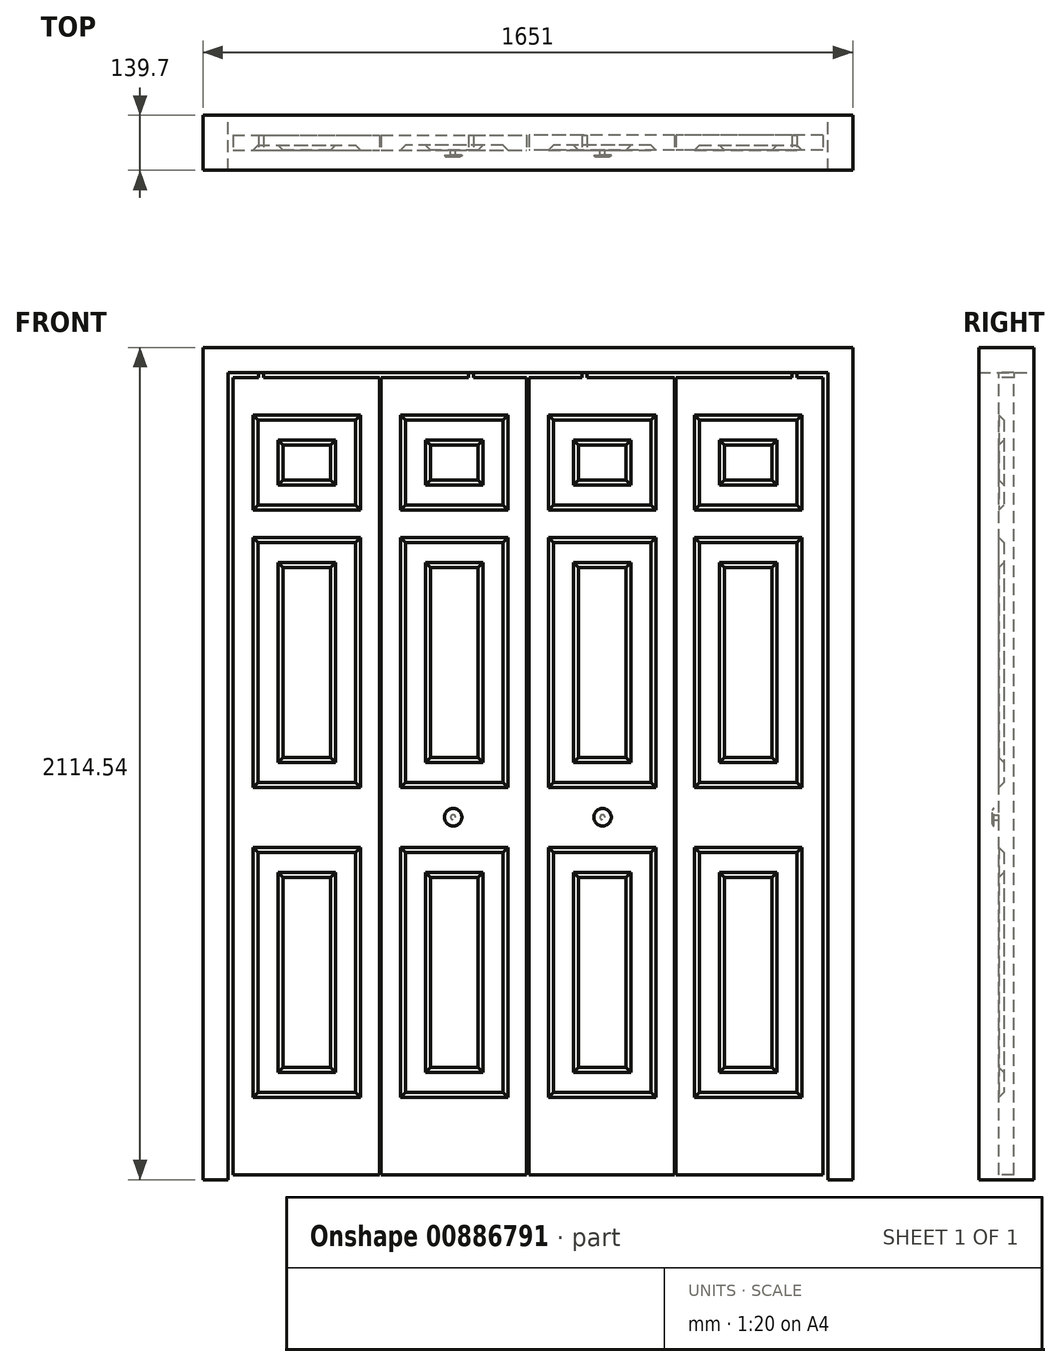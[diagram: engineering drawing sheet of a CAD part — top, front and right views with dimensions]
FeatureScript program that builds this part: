
annotation { "Feature Type Name" : "Feature", "Feature Type Description" : "" }
export const myFeature = defineFeature(function(context is Context, id is Id, definition is map)
    precondition{}
    {
        {
            var Q0;
            Q0=qCreatedBy(makeId("Front.planeOp"),FACE);
            var sketch = newSketch(context, id + "F0", { "sketchPlane" : qUnion([Q0])});
            skLineSegment(sketch, "E0.bottom", {"start": v(-825.5, 1057.28) * mm, "end": v(825.5, 1057.28) * mm});
            skLineSegment(sketch, "E0.top", {"start": v(-825.5, -1057.28) * mm, "end": v(-762, -1057.28) * mm});
            skLineSegment(sketch, "E0.left", {"start": v(-825.5, 1057.28) * mm, "end": v(-825.5, -1057.28) * mm});
            skLineSegment(sketch, "E0.right", {"start": v(825.5, 1057.28) * mm, "end": v(825.5, -1057.28) * mm});
            skPoint(sketch, "E0.middle", {"position": v(0, 0) * mm});
            skLineSegment(sketch, "E1", {"start": v(-762, -1057.28) * mm, "end": v(-762, 993.78) * mm});
            skLineSegment(sketch, "E2", {"start": v(-762, 993.78) * mm, "end": v(762, 993.78) * mm});
            skLineSegment(sketch, "E3", {"start": v(762, 993.78) * mm, "end": v(762, -1057.28) * mm});
            skLineSegment(sketch, "E4.trimOffspring", {"start": v(762, -1057.28) * mm, "end": v(825.5, -1057.28) * mm});
            skLineSegment(sketch, "E5", {"start": v(-762, -1057.28) * mm, "end": v(762, -1057.28) * mm});
            skSolve(sketch);
        }
        {
            var Q0;
            Q0=makeQuery(id+"F0.imprint","IMPRINT",FACE,{"disambiguationData":[TD([[makeQuery(id+"F0.imprint","IMPRINT",EDGE,{"derivedFrom":sQuery(id+"F0.wireOp",EDGE,"E0.bottom")}),-1.0]])]});
            extrude(context, id + "F1", {"entities" : qUnion([Q0]), "endBound" : BoundingType.SYMMETRIC, "depth" : 139.7 * mm, "offsetDistance" : 25.4 * mm});
        }
        {
            var Q0;
            Q0=makeQuery(id+"F0.imprint","IMPRINT",FACE,{"disambiguationData":[TD([[makeQuery(id+"F0.imprint","IMPRINT",EDGE,{"derivedFrom":sQuery(id+"F0.wireOp",EDGE,"E1")}),-1.0]])]});
            extrude(context, id + "F2", {"entities" : qUnion([Q0]), "operationType" : NewBodyOperationType.ADD, "endBound" : BoundingType.SYMMETRIC, "depth" : 38.1 * mm, "offsetDistance" : 25.4 * mm});
        }
        {
            var Q0;
            Q0=makeQuery(id+"F2.opExtrude","CAP_FACE",FACE,{"disambiguationData":[OSD([sQuery(id+"F0.wireOp",EDGE,"E1"),sQuery(id+"F0.wireOp",EDGE,"E2"),sQuery(id+"F0.wireOp",EDGE,"E3"),sQuery(id+"F0.wireOp",EDGE,"E5")])],"isStart":false});
            var sketch = newSketch(context, id + "F3", { "sketchPlane" : qUnion([Q0])});
            skLineSegment(sketch, "E6", {"start": v(-749.3, -1044.58) * mm, "end": v(-749.3, 981.08) * mm});
            skLineSegment(sketch, "E7", {"start": v(-749.3, 981.08) * mm, "end": v(-683.85, 981.08) * mm});
            skLineSegment(sketch, "E8", {"start": v(-683.85, 981.08) * mm, "end": v(-683.85, 993.78) * mm});
            skLineSegment(sketch, "E9", {"start": v(-671.15, 993.78) * mm, "end": v(-671.15, 981.08) * mm});
            skLineSegment(sketch, "E10", {"start": v(-671.15, 981.08) * mm, "end": v(-150.18, 981.08) * mm});
            skLineSegment(sketch, "E11", {"start": v(-150.18, 981.08) * mm, "end": v(-150.18, 993.78) * mm});
            skLineSegment(sketch, "E12", {"start": v(-137.48, 993.78) * mm, "end": v(-137.48, 981.08) * mm});
            skLineSegment(sketch, "E13", {"start": v(-137.48, 981.08) * mm, "end": v(0, 981.08) * mm});
            skLineSegment(sketch, "E14", {"start": v(-749.3, -1044.58) * mm, "end": v(0, -1044.58) * mm});
            skLineSegment(sketch, "E15", {"start": v(0, 241.91) * mm, "end": v(0, -156.2) * mm});
            skLineSegment(sketch, "E16.MirrorCS", {"start": v(137.48, 993.78) * mm, "end": v(137.48, 981.08) * mm});
            skLineSegment(sketch, "E17.MirrorCS", {"start": v(671.15, 993.78) * mm, "end": v(671.15, 981.08) * mm});
            skLineSegment(sketch, "E18.MirrorCS", {"start": v(749.3, 981.08) * mm, "end": v(683.85, 981.08) * mm});
            skLineSegment(sketch, "E19.MirrorCS", {"start": v(683.85, 981.08) * mm, "end": v(683.85, 993.78) * mm});
            skLineSegment(sketch, "E20.MirrorCS", {"start": v(150.18, 981.08) * mm, "end": v(150.18, 993.78) * mm});
            skLineSegment(sketch, "E21.MirrorCS", {"start": v(671.15, 981.08) * mm, "end": v(150.18, 981.08) * mm});
            skLineSegment(sketch, "E22.MirrorCS", {"start": v(137.48, 981.08) * mm, "end": v(0, 981.08) * mm});
            skLineSegment(sketch, "E23.MirrorCS", {"start": v(749.3, -1044.58) * mm, "end": v(749.3, 981.08) * mm});
            skLineSegment(sketch, "E24.MirrorCS", {"start": v(749.3, -1044.58) * mm, "end": v(0, -1044.58) * mm});
            skLineSegment(sketch, "E25", {"start": v(-3.17, -1044.58) * mm, "end": v(-3.18, 981.08) * mm});
            skLineSegment(sketch, "E26", {"start": v(3.18, -1044.58) * mm, "end": v(3.17, 981.08) * mm});
            skSolve(sketch);
        }
        {
            var Q0;
            Q0 = qSketchRegion(id + "F3", true);
            var Q1;
            {var subQ7=sQuery(id+"F3.wireOp",EDGE,"E6");Q1=makeQuery(id+"F3.imprint","IMPRINT",FACE,{"disambiguationData":[TD([[makeQuery(id+"F3.imprint","IMPRINT",EDGE,{"derivedFrom":subQ7}),1.0]])]});}
            var Q2;
            {var subQ0=sQuery(id+"F3.wireOp",EDGE,"E17.MirrorCS");Q2=makeQuery(id+"F3.imprint","IMPRINT",FACE,{"disambiguationData":[TD([[makeQuery(id+"F3.imprint","IMPRINT",EDGE,{"derivedFrom":subQ0}),-1.0]])]});}
            var Q3;
            {var subQ4=sQuery(id+"F3.wireOp",EDGE,"E12");Q3=makeQuery(id+"F3.imprint","IMPRINT",FACE,{"disambiguationData":[TD([[makeQuery(id+"F3.imprint","IMPRINT",EDGE,{"derivedFrom":subQ4}),1.0]])]});}
            var Q4;
            {var subQ0=sQuery(id+"F3.wireOp",EDGE,"E9");Q4=makeQuery(id+"F3.imprint","IMPRINT",FACE,{"disambiguationData":[TD([[makeQuery(id+"F3.imprint","IMPRINT",EDGE,{"derivedFrom":subQ0}),1.0]])]});}
            extrude(context, id + "F4", {"entities" : qUnion([Q0, Q1, Q2, Q3, Q4]), "operationType" : NewBodyOperationType.REMOVE, "endBound" : BoundingType.THROUGH_ALL, "oppositeDirection" : true, "depth" : 25.4 * mm, "offsetDistance" : 25.4 * mm});
        }
        {
            var Q0;
            {var subQ1=sQuery(id+"F0.wireOp",EDGE,"E2");var subQ6=sQuery(id+"F0.wireOp",EDGE,"E1");var subQ7=sQuery(id+"F0.wireOp",EDGE,"E3");Q0=makeQuery(id+"F4.boolean.opBoolean","SPLIT",FACE,{"disambiguationData":[TD([makeQuery(id+"F4.opExtrude","SWEPT_FACE",FACE,{"disambiguationData":[OSD([sQuery(id+"F3.wireOp",EDGE,"E6")])]})])],"derivedFrom":makeQuery(id+"F2.opExtrude","CAP_FACE",FACE,{"disambiguationData":[OSD([subQ6,subQ1,subQ7,sQuery(id+"F0.wireOp",EDGE,"E5")])],"isStart":false})});}
            var sketch = newSketch(context, id + "F5", { "sketchPlane" : qUnion([Q0])});
            skLineSegment(sketch, "E27.bottom", {"start": v(-685.8, 873.12) * mm, "end": v(-438.15, 873.12) * mm});
            skLineSegment(sketch, "E27.top", {"start": v(-685.8, 657.23) * mm, "end": v(-438.15, 657.23) * mm});
            skLineSegment(sketch, "E27.left", {"start": v(-685.8, 873.12) * mm, "end": v(-685.8, 657.23) * mm});
            skLineSegment(sketch, "E27.right", {"start": v(-438.15, 873.12) * mm, "end": v(-438.15, 657.23) * mm});
            skLineSegment(sketch, "E28.bottom", {"start": v(-685.8, 561.98) * mm, "end": v(-438.15, 561.98) * mm});
            skLineSegment(sketch, "E28.top", {"start": v(-685.8, -47.62) * mm, "end": v(-438.15, -47.62) * mm});
            skLineSegment(sketch, "E28.left", {"start": v(-685.8, 561.98) * mm, "end": v(-685.8, -47.62) * mm});
            skLineSegment(sketch, "E28.right", {"start": v(-438.15, 561.98) * mm, "end": v(-438.15, -47.62) * mm});
            skLineSegment(sketch, "E29.bottom", {"start": v(-438.15, -225.42) * mm, "end": v(-685.8, -225.42) * mm});
            skLineSegment(sketch, "E29.top", {"start": v(-438.15, -835.02) * mm, "end": v(-685.8, -835.02) * mm});
            skLineSegment(sketch, "E29.left", {"start": v(-438.15, -225.42) * mm, "end": v(-438.15, -835.02) * mm});
            skLineSegment(sketch, "E29.right", {"start": v(-685.8, -225.42) * mm, "end": v(-685.8, -835.02) * mm});
            skLineSegment(sketch, "E30", {"start": v(-374.65, 943.32) * mm, "end": v(-374.65, -1018.84) * mm});
            skLineSegment(sketch, "E31.0", {"start": v(-635, 511.18) * mm, "end": v(-635, 3.18) * mm});
            skLineSegment(sketch, "E31.1", {"start": v(-635, 511.18) * mm, "end": v(-488.95, 511.18) * mm});
            skLineSegment(sketch, "E31.2", {"start": v(-488.95, 511.18) * mm, "end": v(-488.95, 3.18) * mm});
            skLineSegment(sketch, "E31.3", {"start": v(-635, 3.18) * mm, "end": v(-488.95, 3.18) * mm});
            skLineSegment(sketch, "E32.0", {"start": v(-635, 822.33) * mm, "end": v(-635, 708.03) * mm});
            skLineSegment(sketch, "E32.1", {"start": v(-635, 822.33) * mm, "end": v(-488.95, 822.33) * mm});
            skLineSegment(sketch, "E32.2", {"start": v(-488.95, 822.33) * mm, "end": v(-488.95, 708.03) * mm});
            skLineSegment(sketch, "E32.3", {"start": v(-635, 708.03) * mm, "end": v(-488.95, 708.03) * mm});
            skLineSegment(sketch, "E33.0", {"start": v(-635, -276.22) * mm, "end": v(-635, -784.22) * mm});
            skLineSegment(sketch, "E33.1", {"start": v(-488.95, -276.22) * mm, "end": v(-635, -276.22) * mm});
            skLineSegment(sketch, "E33.2", {"start": v(-488.95, -276.22) * mm, "end": v(-488.95, -784.22) * mm});
            skLineSegment(sketch, "E33.3", {"start": v(-488.95, -784.22) * mm, "end": v(-635, -784.22) * mm});
            skLineSegment(sketch, "E34.MirrorCS", {"start": v(-311.15, -225.42) * mm, "end": v(-311.15, -835.02) * mm});
            skLineSegment(sketch, "E35.MirrorCS", {"start": v(-260.35, 511.18) * mm, "end": v(-260.35, 3.18) * mm});
            skLineSegment(sketch, "E36.MirrorCS", {"start": v(-311.15, -835.02) * mm, "end": v(-63.5, -835.02) * mm});
            skLineSegment(sketch, "E37.MirrorCS", {"start": v(-114.3, 3.18) * mm, "end": v(-260.35, 3.18) * mm});
            skLineSegment(sketch, "E38.MirrorCS", {"start": v(-63.5, 561.98) * mm, "end": v(-311.15, 561.98) * mm});
            skLineSegment(sketch, "E39.MirrorCS", {"start": v(-63.5, 873.13) * mm, "end": v(-63.5, 657.23) * mm});
            skLineSegment(sketch, "E40.MirrorCS", {"start": v(-311.15, 873.12) * mm, "end": v(-311.15, 657.23) * mm});
            skLineSegment(sketch, "E41.MirrorCS", {"start": v(-63.5, 657.23) * mm, "end": v(-311.15, 657.23) * mm});
            skLineSegment(sketch, "E42.MirrorCS", {"start": v(-260.35, -276.22) * mm, "end": v(-114.3, -276.22) * mm});
            skLineSegment(sketch, "E43.MirrorCS", {"start": v(-114.3, 822.33) * mm, "end": v(-260.35, 822.33) * mm});
            skLineSegment(sketch, "E44.MirrorCS", {"start": v(-114.3, 511.18) * mm, "end": v(-114.3, 3.18) * mm});
            skLineSegment(sketch, "E45.MirrorCS", {"start": v(-63.5, -225.42) * mm, "end": v(-63.5, -835.02) * mm});
            skLineSegment(sketch, "E46.MirrorCS", {"start": v(-63.5, 873.13) * mm, "end": v(-311.15, 873.13) * mm});
            skLineSegment(sketch, "E47.MirrorCS", {"start": v(-260.35, -784.22) * mm, "end": v(-114.3, -784.22) * mm});
            skLineSegment(sketch, "E48.MirrorCS", {"start": v(-311.15, 561.98) * mm, "end": v(-311.15, -47.62) * mm});
            skLineSegment(sketch, "E49.MirrorCS", {"start": v(-63.5, -47.62) * mm, "end": v(-311.15, -47.62) * mm});
            skLineSegment(sketch, "E50.MirrorCS", {"start": v(-63.5, 561.98) * mm, "end": v(-63.5, -47.62) * mm});
            skLineSegment(sketch, "E51.MirrorCS", {"start": v(-260.35, 822.33) * mm, "end": v(-260.35, 708.03) * mm});
            skLineSegment(sketch, "E52.MirrorCS", {"start": v(-311.15, -225.42) * mm, "end": v(-63.5, -225.42) * mm});
            skLineSegment(sketch, "E53.MirrorCS", {"start": v(-260.35, -276.22) * mm, "end": v(-260.35, -784.22) * mm});
            skLineSegment(sketch, "E54.MirrorCS", {"start": v(-114.3, -276.22) * mm, "end": v(-114.3, -784.22) * mm});
            skLineSegment(sketch, "E55.MirrorCS", {"start": v(-114.3, 511.18) * mm, "end": v(-260.35, 511.18) * mm});
            skLineSegment(sketch, "E56.MirrorCS", {"start": v(-114.3, 822.33) * mm, "end": v(-114.3, 708.03) * mm});
            skLineSegment(sketch, "E57.MirrorCS", {"start": v(-114.3, 708.03) * mm, "end": v(-260.35, 708.03) * mm});
            skLineSegment(sketch, "E58", {"start": v(-376.24, -1044.58) * mm, "end": v(-376.24, 981.08) * mm});
            skLineSegment(sketch, "E59", {"start": v(-373.06, 981.08) * mm, "end": v(-373.06, -1044.58) * mm});
            skSolve(sketch);
        }
        {
            var Q0;
            {var subQ2=sQuery(id+"F0.wireOp",EDGE,"E2");var subQ4=sQuery(id+"F3.wireOp",EDGE,"E16.MirrorCS");var subQ6=sQuery(id+"F0.wireOp",EDGE,"E1");var subQ7=sQuery(id+"F0.wireOp",EDGE,"E3");Q0=makeQuery(id+"F4.boolean.opBoolean","SPLIT",FACE,{"disambiguationData":[TD([makeQuery(id+"F4.opExtrude","SWEPT_FACE",FACE,{"disambiguationData":[OSD([subQ4])]})])],"derivedFrom":makeQuery(id+"F2.opExtrude","CAP_FACE",FACE,{"disambiguationData":[OSD([subQ6,subQ2,subQ7,sQuery(id+"F0.wireOp",EDGE,"E5")])],"isStart":false})});}
            var sketch = newSketch(context, id + "F6", { "sketchPlane" : qUnion([Q0])});
            skLineSegment(sketch, "E60.bottom", {"start": v(65.1, 873.13) * mm, "end": v(312.74, 873.13) * mm});
            skLineSegment(sketch, "E60.top", {"start": v(65.1, 657.23) * mm, "end": v(312.74, 657.23) * mm});
            skLineSegment(sketch, "E60.left", {"start": v(65.1, 873.13) * mm, "end": v(65.1, 657.23) * mm});
            skLineSegment(sketch, "E60.right", {"start": v(312.74, 873.13) * mm, "end": v(312.74, 657.23) * mm});
            skLineSegment(sketch, "E61.bottom", {"start": v(65.1, 561.98) * mm, "end": v(312.74, 561.98) * mm});
            skLineSegment(sketch, "E61.top", {"start": v(65.1, -47.62) * mm, "end": v(312.74, -47.62) * mm});
            skLineSegment(sketch, "E61.left", {"start": v(65.1, 561.98) * mm, "end": v(65.1, -47.62) * mm});
            skLineSegment(sketch, "E61.right", {"start": v(312.74, 561.98) * mm, "end": v(312.74, -47.62) * mm});
            skLineSegment(sketch, "E62.bottom", {"start": v(312.74, -225.42) * mm, "end": v(65.1, -225.42) * mm});
            skLineSegment(sketch, "E62.top", {"start": v(312.74, -835.02) * mm, "end": v(65.1, -835.02) * mm});
            skLineSegment(sketch, "E62.left", {"start": v(312.74, -225.42) * mm, "end": v(312.74, -835.02) * mm});
            skLineSegment(sketch, "E62.right", {"start": v(65.1, -225.42) * mm, "end": v(65.1, -835.02) * mm});
            skLineSegment(sketch, "E63", {"start": v(374.65, 751.87) * mm, "end": v(374.65, -1210.3) * mm});
            skLineSegment(sketch, "E64.0", {"start": v(115.9, 511.18) * mm, "end": v(115.9, 3.18) * mm});
            skLineSegment(sketch, "E64.1", {"start": v(115.9, 511.18) * mm, "end": v(261.94, 511.18) * mm});
            skLineSegment(sketch, "E64.2", {"start": v(261.94, 511.18) * mm, "end": v(261.94, 3.18) * mm});
            skLineSegment(sketch, "E64.3", {"start": v(115.9, 3.18) * mm, "end": v(261.94, 3.18) * mm});
            skLineSegment(sketch, "E65.0", {"start": v(115.9, 822.33) * mm, "end": v(115.9, 708.03) * mm});
            skLineSegment(sketch, "E65.1", {"start": v(115.9, 822.33) * mm, "end": v(261.94, 822.33) * mm});
            skLineSegment(sketch, "E65.2", {"start": v(261.94, 822.33) * mm, "end": v(261.94, 708.03) * mm});
            skLineSegment(sketch, "E65.3", {"start": v(115.9, 708.03) * mm, "end": v(261.94, 708.03) * mm});
            skLineSegment(sketch, "E66.0", {"start": v(115.9, -276.22) * mm, "end": v(115.9, -784.22) * mm});
            skLineSegment(sketch, "E66.1", {"start": v(261.94, -276.22) * mm, "end": v(115.9, -276.22) * mm});
            skLineSegment(sketch, "E66.2", {"start": v(261.94, -276.22) * mm, "end": v(261.94, -784.22) * mm});
            skLineSegment(sketch, "E66.3", {"start": v(261.94, -784.22) * mm, "end": v(115.9, -784.22) * mm});
            skLineSegment(sketch, "E67.MirrorCS", {"start": v(436.56, -225.42) * mm, "end": v(436.56, -835.02) * mm});
            skLineSegment(sketch, "E68.MirrorCS", {"start": v(487.36, 511.18) * mm, "end": v(487.36, 3.18) * mm});
            skLineSegment(sketch, "E69.MirrorCS", {"start": v(436.56, -835.02) * mm, "end": v(684.2, -835.02) * mm});
            skLineSegment(sketch, "E70.MirrorCS", {"start": v(633.4, 3.18) * mm, "end": v(487.36, 3.18) * mm});
            skLineSegment(sketch, "E71.MirrorCS", {"start": v(684.2, 561.98) * mm, "end": v(436.56, 561.98) * mm});
            skLineSegment(sketch, "E72.MirrorCS", {"start": v(684.2, 873.13) * mm, "end": v(684.2, 657.23) * mm});
            skLineSegment(sketch, "E73.MirrorCS", {"start": v(436.56, 873.13) * mm, "end": v(436.56, 657.23) * mm});
            skLineSegment(sketch, "E74.MirrorCS", {"start": v(684.2, 657.23) * mm, "end": v(436.56, 657.23) * mm});
            skLineSegment(sketch, "E75.MirrorCS", {"start": v(487.36, -276.22) * mm, "end": v(633.4, -276.22) * mm});
            skLineSegment(sketch, "E76.MirrorCS", {"start": v(633.4, 822.33) * mm, "end": v(487.36, 822.33) * mm});
            skLineSegment(sketch, "E77.MirrorCS", {"start": v(633.4, 511.18) * mm, "end": v(633.4, 3.18) * mm});
            skLineSegment(sketch, "E78.MirrorCS", {"start": v(684.2, -225.42) * mm, "end": v(684.2, -835.02) * mm});
            skLineSegment(sketch, "E79.MirrorCS", {"start": v(684.2, 873.13) * mm, "end": v(436.56, 873.13) * mm});
            skLineSegment(sketch, "E80.MirrorCS", {"start": v(487.36, -784.22) * mm, "end": v(633.4, -784.22) * mm});
            skLineSegment(sketch, "E81.MirrorCS", {"start": v(436.56, 561.98) * mm, "end": v(436.56, -47.62) * mm});
            skLineSegment(sketch, "E82.MirrorCS", {"start": v(684.2, -47.62) * mm, "end": v(436.56, -47.62) * mm});
            skLineSegment(sketch, "E83.MirrorCS", {"start": v(684.2, 561.98) * mm, "end": v(684.2, -47.62) * mm});
            skLineSegment(sketch, "E84.MirrorCS", {"start": v(487.36, 822.33) * mm, "end": v(487.36, 708.03) * mm});
            skLineSegment(sketch, "E85.MirrorCS", {"start": v(436.56, -225.42) * mm, "end": v(684.2, -225.42) * mm});
            skLineSegment(sketch, "E86.MirrorCS", {"start": v(487.36, -276.22) * mm, "end": v(487.36, -784.22) * mm});
            skLineSegment(sketch, "E87.MirrorCS", {"start": v(633.4, -276.22) * mm, "end": v(633.4, -784.22) * mm});
            skLineSegment(sketch, "E88.MirrorCS", {"start": v(633.4, 511.18) * mm, "end": v(487.36, 511.18) * mm});
            skLineSegment(sketch, "E89.MirrorCS", {"start": v(633.4, 822.33) * mm, "end": v(633.4, 708.03) * mm});
            skLineSegment(sketch, "E90.MirrorCS", {"start": v(633.4, 708.03) * mm, "end": v(487.36, 708.03) * mm});
            skLineSegment(sketch, "E91", {"start": v(373.06, 981.08) * mm, "end": v(373.06, -1044.58) * mm});
            skLineSegment(sketch, "E92", {"start": v(376.24, -1044.58) * mm, "end": v(376.24, 981.08) * mm});
            skSolve(sketch);
        }
        {
            var Q0;
            {var subQ0=sQuery(id+"F5.wireOp",EDGE,"E58");Q0=makeQuery(id+"F5.imprint","IMPRINT",FACE,{"disambiguationData":[TD([[makeQuery(id+"F5.imprint","IMPRINT",EDGE,{"derivedFrom":subQ0}),-1.0]])]});}
            var Q1;
            {var subQ0=sQuery(id+"F6.wireOp",EDGE,"E91");Q1=makeQuery(id+"F6.imprint","IMPRINT",FACE,{"disambiguationData":[TD([[makeQuery(id+"F6.imprint","IMPRINT",EDGE,{"derivedFrom":subQ0}),1.0]])]});}
            extrude(context, id + "F7", {"entities" : qUnion([Q0, Q1]), "operationType" : NewBodyOperationType.REMOVE, "endBound" : BoundingType.THROUGH_ALL, "oppositeDirection" : true, "depth" : 25.4 * mm, "offsetDistance" : 25.4 * mm});
        }
        {
            var Q0;
            Q0=makeQuery(id+"F5.imprint","IMPRINT",FACE,{"disambiguationData":[TD([[makeQuery(id+"F5.imprint","IMPRINT",EDGE,{"derivedFrom":sQuery(id+"F5.wireOp",EDGE,"E27.bottom")}),-1.0]])]});
            var Q1;
            Q1=makeQuery(id+"F5.imprint","IMPRINT",FACE,{"disambiguationData":[TD([[makeQuery(id+"F5.imprint","IMPRINT",EDGE,{"derivedFrom":sQuery(id+"F5.wireOp",EDGE,"E28.bottom")}),-1.0]])]});
            var Q2;
            Q2=makeQuery(id+"F5.imprint","IMPRINT",FACE,{"disambiguationData":[TD([[makeQuery(id+"F5.imprint","IMPRINT",EDGE,{"derivedFrom":sQuery(id+"F5.wireOp",EDGE,"E29.bottom")}),1.0]])]});
            var Q3;
            Q3=makeQuery(id+"F5.imprint","IMPRINT",FACE,{"disambiguationData":[TD([[makeQuery(id+"F5.imprint","IMPRINT",EDGE,{"derivedFrom":sQuery(id+"F5.wireOp",EDGE,"E34.MirrorCS")}),1.0]])]});
            var Q4;
            Q4=makeQuery(id+"F5.imprint","IMPRINT",FACE,{"disambiguationData":[TD([[makeQuery(id+"F5.imprint","IMPRINT",EDGE,{"derivedFrom":sQuery(id+"F5.wireOp",EDGE,"E35.MirrorCS")}),-1.0]])]});
            var Q5;
            Q5=makeQuery(id+"F5.imprint","IMPRINT",FACE,{"disambiguationData":[TD([[makeQuery(id+"F5.imprint","IMPRINT",EDGE,{"derivedFrom":sQuery(id+"F5.wireOp",EDGE,"E39.MirrorCS")}),-1.0]])]});
            var Q6;
            Q6=makeQuery(id+"F6.imprint","IMPRINT",FACE,{"disambiguationData":[TD([[makeQuery(id+"F6.imprint","IMPRINT",EDGE,{"derivedFrom":sQuery(id+"F6.wireOp",EDGE,"E60.bottom")}),-1.0]])]});
            var Q7;
            Q7=makeQuery(id+"F6.imprint","IMPRINT",FACE,{"disambiguationData":[TD([[makeQuery(id+"F6.imprint","IMPRINT",EDGE,{"derivedFrom":sQuery(id+"F6.wireOp",EDGE,"E61.bottom")}),-1.0]])]});
            var Q8;
            Q8=makeQuery(id+"F6.imprint","IMPRINT",FACE,{"disambiguationData":[TD([[makeQuery(id+"F6.imprint","IMPRINT",EDGE,{"derivedFrom":sQuery(id+"F6.wireOp",EDGE,"E62.bottom")}),1.0]])]});
            var Q9;
            Q9=makeQuery(id+"F6.imprint","IMPRINT",FACE,{"disambiguationData":[TD([[makeQuery(id+"F6.imprint","IMPRINT",EDGE,{"derivedFrom":sQuery(id+"F6.wireOp",EDGE,"E67.MirrorCS")}),1.0]])]});
            var Q10;
            Q10=makeQuery(id+"F6.imprint","IMPRINT",FACE,{"disambiguationData":[TD([[makeQuery(id+"F6.imprint","IMPRINT",EDGE,{"derivedFrom":sQuery(id+"F6.wireOp",EDGE,"E68.MirrorCS")}),-1.0]])]});
            var Q11;
            Q11=makeQuery(id+"F6.imprint","IMPRINT",FACE,{"disambiguationData":[TD([[makeQuery(id+"F6.imprint","IMPRINT",EDGE,{"derivedFrom":sQuery(id+"F6.wireOp",EDGE,"E72.MirrorCS")}),-1.0]])]});
            extrude(context, id + "F8", {"entities" : qUnion([Q0, Q1, Q2, Q3, Q4, Q5, Q6, Q7, Q8, Q9, Q10, Q11]), "operationType" : NewBodyOperationType.REMOVE, "oppositeDirection" : true, "depth" : 12.7 * mm, "offsetDistance" : 25.4 * mm});
        }
        {
            var Q0;
            {var subQ2=sQuery(id+"F0.wireOp",EDGE,"E2");var subQ5=makeQuery(id+"F4.opExtrude","SWEPT_FACE",FACE,{"disambiguationData":[OSD([sQuery(id+"F3.wireOp",EDGE,"E6")])]});var subQ13=sQuery(id+"F0.wireOp",EDGE,"E1");var subQ14=sQuery(id+"F0.wireOp",EDGE,"E3");Q0=makeQuery(id+"F8.boolean.opBoolean","SPLIT",FACE,{"disambiguationData":[TD([makeQuery(id+"F8.opExtrude","SWEPT_FACE",FACE,{"disambiguationData":[OSD([sQuery(id+"F5.wireOp",EDGE,"E31.0")])]})])],"derivedFrom":makeQuery(id+"F7.boolean.opBoolean","SPLIT",FACE,{"disambiguationData":[TD([makeQuery(id+"F4.boolean.opBoolean","COPY",FACE,{"derivedFrom":subQ5})])],"derivedFrom":makeQuery(id+"F4.boolean.opBoolean","SPLIT",FACE,{"disambiguationData":[TD([subQ5])],"derivedFrom":makeQuery(id+"F2.opExtrude","CAP_FACE",FACE,{"disambiguationData":[OSD([subQ13,subQ2,subQ14,sQuery(id+"F0.wireOp",EDGE,"E5")])],"isStart":false})})})});}
            var Q1;
            {var subQ2=sQuery(id+"F3.wireOp",EDGE,"E11");var subQ3=makeQuery(id+"F4.opExtrude","SWEPT_FACE",FACE,{"disambiguationData":[OSD([subQ2])]});var subQ5=sQuery(id+"F0.wireOp",EDGE,"E2");var subQ13=sQuery(id+"F0.wireOp",EDGE,"E1");var subQ14=sQuery(id+"F0.wireOp",EDGE,"E3");Q1=makeQuery(id+"F8.boolean.opBoolean","SPLIT",FACE,{"disambiguationData":[TD([makeQuery(id+"F8.opExtrude","SWEPT_FACE",FACE,{"disambiguationData":[OSD([sQuery(id+"F5.wireOp",EDGE,"E35.MirrorCS")])]})])],"derivedFrom":makeQuery(id+"F7.boolean.opBoolean","SPLIT",FACE,{"disambiguationData":[TD([makeQuery(id+"F4.boolean.opBoolean","COPY",FACE,{"derivedFrom":subQ3})])],"derivedFrom":makeQuery(id+"F4.boolean.opBoolean","SPLIT",FACE,{"disambiguationData":[TD([makeQuery(id+"F4.opExtrude","SWEPT_FACE",FACE,{"disambiguationData":[OSD([sQuery(id+"F3.wireOp",EDGE,"E6")])]})])],"derivedFrom":makeQuery(id+"F2.opExtrude","CAP_FACE",FACE,{"disambiguationData":[OSD([subQ13,subQ5,subQ14,sQuery(id+"F0.wireOp",EDGE,"E5")])],"isStart":false})})})});}
            var Q2;
            {var subQ2=sQuery(id+"F3.wireOp",EDGE,"E11");var subQ3=makeQuery(id+"F4.opExtrude","SWEPT_FACE",FACE,{"disambiguationData":[OSD([subQ2])]});var subQ5=sQuery(id+"F0.wireOp",EDGE,"E2");var subQ13=sQuery(id+"F0.wireOp",EDGE,"E1");var subQ14=sQuery(id+"F0.wireOp",EDGE,"E3");Q2=makeQuery(id+"F8.boolean.opBoolean","SPLIT",FACE,{"disambiguationData":[TD([makeQuery(id+"F8.opExtrude","SWEPT_FACE",FACE,{"disambiguationData":[OSD([sQuery(id+"F5.wireOp",EDGE,"E43.MirrorCS")])]})])],"derivedFrom":makeQuery(id+"F7.boolean.opBoolean","SPLIT",FACE,{"disambiguationData":[TD([makeQuery(id+"F4.boolean.opBoolean","COPY",FACE,{"derivedFrom":subQ3})])],"derivedFrom":makeQuery(id+"F4.boolean.opBoolean","SPLIT",FACE,{"disambiguationData":[TD([makeQuery(id+"F4.opExtrude","SWEPT_FACE",FACE,{"disambiguationData":[OSD([sQuery(id+"F3.wireOp",EDGE,"E6")])]})])],"derivedFrom":makeQuery(id+"F2.opExtrude","CAP_FACE",FACE,{"disambiguationData":[OSD([subQ13,subQ5,subQ14,sQuery(id+"F0.wireOp",EDGE,"E5")])],"isStart":false})})})});}
            var Q3;
            {var subQ2=sQuery(id+"F0.wireOp",EDGE,"E2");var subQ5=makeQuery(id+"F4.opExtrude","SWEPT_FACE",FACE,{"disambiguationData":[OSD([sQuery(id+"F3.wireOp",EDGE,"E6")])]});var subQ13=sQuery(id+"F0.wireOp",EDGE,"E1");var subQ14=sQuery(id+"F0.wireOp",EDGE,"E3");Q3=makeQuery(id+"F8.boolean.opBoolean","SPLIT",FACE,{"disambiguationData":[TD([makeQuery(id+"F8.opExtrude","SWEPT_FACE",FACE,{"disambiguationData":[OSD([sQuery(id+"F5.wireOp",EDGE,"E32.0")])]})])],"derivedFrom":makeQuery(id+"F7.boolean.opBoolean","SPLIT",FACE,{"disambiguationData":[TD([makeQuery(id+"F4.boolean.opBoolean","COPY",FACE,{"derivedFrom":subQ5})])],"derivedFrom":makeQuery(id+"F4.boolean.opBoolean","SPLIT",FACE,{"disambiguationData":[TD([subQ5])],"derivedFrom":makeQuery(id+"F2.opExtrude","CAP_FACE",FACE,{"disambiguationData":[OSD([subQ13,subQ2,subQ14,sQuery(id+"F0.wireOp",EDGE,"E5")])],"isStart":false})})})});}
            var Q4;
            {var subQ2=sQuery(id+"F0.wireOp",EDGE,"E2");var subQ5=makeQuery(id+"F4.opExtrude","SWEPT_FACE",FACE,{"disambiguationData":[OSD([sQuery(id+"F3.wireOp",EDGE,"E6")])]});var subQ13=sQuery(id+"F0.wireOp",EDGE,"E1");var subQ14=sQuery(id+"F0.wireOp",EDGE,"E3");Q4=makeQuery(id+"F8.boolean.opBoolean","SPLIT",FACE,{"disambiguationData":[TD([makeQuery(id+"F8.opExtrude","SWEPT_FACE",FACE,{"disambiguationData":[OSD([sQuery(id+"F5.wireOp",EDGE,"E33.0")])]})])],"derivedFrom":makeQuery(id+"F7.boolean.opBoolean","SPLIT",FACE,{"disambiguationData":[TD([makeQuery(id+"F4.boolean.opBoolean","COPY",FACE,{"derivedFrom":subQ5})])],"derivedFrom":makeQuery(id+"F4.boolean.opBoolean","SPLIT",FACE,{"disambiguationData":[TD([subQ5])],"derivedFrom":makeQuery(id+"F2.opExtrude","CAP_FACE",FACE,{"disambiguationData":[OSD([subQ13,subQ2,subQ14,sQuery(id+"F0.wireOp",EDGE,"E5")])],"isStart":false})})})});}
            var Q5;
            {var subQ2=sQuery(id+"F3.wireOp",EDGE,"E11");var subQ3=makeQuery(id+"F4.opExtrude","SWEPT_FACE",FACE,{"disambiguationData":[OSD([subQ2])]});var subQ5=sQuery(id+"F0.wireOp",EDGE,"E2");var subQ13=sQuery(id+"F0.wireOp",EDGE,"E1");var subQ14=sQuery(id+"F0.wireOp",EDGE,"E3");Q5=makeQuery(id+"F8.boolean.opBoolean","SPLIT",FACE,{"disambiguationData":[TD([makeQuery(id+"F8.opExtrude","SWEPT_FACE",FACE,{"disambiguationData":[OSD([sQuery(id+"F5.wireOp",EDGE,"E42.MirrorCS")])]})])],"derivedFrom":makeQuery(id+"F7.boolean.opBoolean","SPLIT",FACE,{"disambiguationData":[TD([makeQuery(id+"F4.boolean.opBoolean","COPY",FACE,{"derivedFrom":subQ3})])],"derivedFrom":makeQuery(id+"F4.boolean.opBoolean","SPLIT",FACE,{"disambiguationData":[TD([makeQuery(id+"F4.opExtrude","SWEPT_FACE",FACE,{"disambiguationData":[OSD([sQuery(id+"F3.wireOp",EDGE,"E6")])]})])],"derivedFrom":makeQuery(id+"F2.opExtrude","CAP_FACE",FACE,{"disambiguationData":[OSD([subQ13,subQ5,subQ14,sQuery(id+"F0.wireOp",EDGE,"E5")])],"isStart":false})})})});}
            var Q6;
            {var subQ1=sQuery(id+"F3.wireOp",EDGE,"E16.MirrorCS");var subQ2=makeQuery(id+"F4.opExtrude","SWEPT_FACE",FACE,{"disambiguationData":[OSD([subQ1])]});var subQ5=sQuery(id+"F0.wireOp",EDGE,"E2");var subQ13=sQuery(id+"F0.wireOp",EDGE,"E1");var subQ14=sQuery(id+"F0.wireOp",EDGE,"E3");Q6=makeQuery(id+"F8.boolean.opBoolean","SPLIT",FACE,{"disambiguationData":[TD([makeQuery(id+"F8.opExtrude","SWEPT_FACE",FACE,{"disambiguationData":[OSD([sQuery(id+"F6.wireOp",EDGE,"E66.0")])]})])],"derivedFrom":makeQuery(id+"F7.boolean.opBoolean","SPLIT",FACE,{"disambiguationData":[TD([makeQuery(id+"F4.boolean.opBoolean","COPY",FACE,{"derivedFrom":subQ2})])],"derivedFrom":makeQuery(id+"F4.boolean.opBoolean","SPLIT",FACE,{"disambiguationData":[TD([subQ2])],"derivedFrom":makeQuery(id+"F2.opExtrude","CAP_FACE",FACE,{"disambiguationData":[OSD([subQ13,subQ5,subQ14,sQuery(id+"F0.wireOp",EDGE,"E5")])],"isStart":false})})})});}
            var Q7;
            {var subQ1=sQuery(id+"F3.wireOp",EDGE,"E16.MirrorCS");var subQ2=makeQuery(id+"F4.opExtrude","SWEPT_FACE",FACE,{"disambiguationData":[OSD([subQ1])]});var subQ5=sQuery(id+"F0.wireOp",EDGE,"E2");var subQ13=sQuery(id+"F0.wireOp",EDGE,"E1");var subQ14=sQuery(id+"F0.wireOp",EDGE,"E3");Q7=makeQuery(id+"F8.boolean.opBoolean","SPLIT",FACE,{"disambiguationData":[TD([makeQuery(id+"F8.opExtrude","SWEPT_FACE",FACE,{"disambiguationData":[OSD([sQuery(id+"F6.wireOp",EDGE,"E64.0")])]})])],"derivedFrom":makeQuery(id+"F7.boolean.opBoolean","SPLIT",FACE,{"disambiguationData":[TD([makeQuery(id+"F4.boolean.opBoolean","COPY",FACE,{"derivedFrom":subQ2})])],"derivedFrom":makeQuery(id+"F4.boolean.opBoolean","SPLIT",FACE,{"disambiguationData":[TD([subQ2])],"derivedFrom":makeQuery(id+"F2.opExtrude","CAP_FACE",FACE,{"disambiguationData":[OSD([subQ13,subQ5,subQ14,sQuery(id+"F0.wireOp",EDGE,"E5")])],"isStart":false})})})});}
            var Q8;
            {var subQ3=sQuery(id+"F3.wireOp",EDGE,"E17.MirrorCS");var subQ4=makeQuery(id+"F4.opExtrude","SWEPT_FACE",FACE,{"disambiguationData":[OSD([subQ3])]});var subQ5=sQuery(id+"F0.wireOp",EDGE,"E2");var subQ12=sQuery(id+"F3.wireOp",EDGE,"E16.MirrorCS");var subQ13=sQuery(id+"F0.wireOp",EDGE,"E1");var subQ14=sQuery(id+"F0.wireOp",EDGE,"E3");Q8=makeQuery(id+"F8.boolean.opBoolean","SPLIT",FACE,{"disambiguationData":[TD([makeQuery(id+"F8.opExtrude","SWEPT_FACE",FACE,{"disambiguationData":[OSD([sQuery(id+"F6.wireOp",EDGE,"E75.MirrorCS")])]})])],"derivedFrom":makeQuery(id+"F7.boolean.opBoolean","SPLIT",FACE,{"disambiguationData":[TD([makeQuery(id+"F4.boolean.opBoolean","COPY",FACE,{"derivedFrom":subQ4})])],"derivedFrom":makeQuery(id+"F4.boolean.opBoolean","SPLIT",FACE,{"disambiguationData":[TD([makeQuery(id+"F4.opExtrude","SWEPT_FACE",FACE,{"disambiguationData":[OSD([subQ12])]})])],"derivedFrom":makeQuery(id+"F2.opExtrude","CAP_FACE",FACE,{"disambiguationData":[OSD([subQ13,subQ5,subQ14,sQuery(id+"F0.wireOp",EDGE,"E5")])],"isStart":false})})})});}
            var Q9;
            {var subQ3=sQuery(id+"F3.wireOp",EDGE,"E17.MirrorCS");var subQ4=makeQuery(id+"F4.opExtrude","SWEPT_FACE",FACE,{"disambiguationData":[OSD([subQ3])]});var subQ5=sQuery(id+"F0.wireOp",EDGE,"E2");var subQ12=sQuery(id+"F3.wireOp",EDGE,"E16.MirrorCS");var subQ13=sQuery(id+"F0.wireOp",EDGE,"E1");var subQ14=sQuery(id+"F0.wireOp",EDGE,"E3");Q9=makeQuery(id+"F8.boolean.opBoolean","SPLIT",FACE,{"disambiguationData":[TD([makeQuery(id+"F8.opExtrude","SWEPT_FACE",FACE,{"disambiguationData":[OSD([sQuery(id+"F6.wireOp",EDGE,"E68.MirrorCS")])]})])],"derivedFrom":makeQuery(id+"F7.boolean.opBoolean","SPLIT",FACE,{"disambiguationData":[TD([makeQuery(id+"F4.boolean.opBoolean","COPY",FACE,{"derivedFrom":subQ4})])],"derivedFrom":makeQuery(id+"F4.boolean.opBoolean","SPLIT",FACE,{"disambiguationData":[TD([makeQuery(id+"F4.opExtrude","SWEPT_FACE",FACE,{"disambiguationData":[OSD([subQ12])]})])],"derivedFrom":makeQuery(id+"F2.opExtrude","CAP_FACE",FACE,{"disambiguationData":[OSD([subQ13,subQ5,subQ14,sQuery(id+"F0.wireOp",EDGE,"E5")])],"isStart":false})})})});}
            var Q10;
            {var subQ3=sQuery(id+"F3.wireOp",EDGE,"E17.MirrorCS");var subQ4=makeQuery(id+"F4.opExtrude","SWEPT_FACE",FACE,{"disambiguationData":[OSD([subQ3])]});var subQ5=sQuery(id+"F0.wireOp",EDGE,"E2");var subQ12=sQuery(id+"F3.wireOp",EDGE,"E16.MirrorCS");var subQ13=sQuery(id+"F0.wireOp",EDGE,"E1");var subQ14=sQuery(id+"F0.wireOp",EDGE,"E3");Q10=makeQuery(id+"F8.boolean.opBoolean","SPLIT",FACE,{"disambiguationData":[TD([makeQuery(id+"F8.opExtrude","SWEPT_FACE",FACE,{"disambiguationData":[OSD([sQuery(id+"F6.wireOp",EDGE,"E76.MirrorCS")])]})])],"derivedFrom":makeQuery(id+"F7.boolean.opBoolean","SPLIT",FACE,{"disambiguationData":[TD([makeQuery(id+"F4.boolean.opBoolean","COPY",FACE,{"derivedFrom":subQ4})])],"derivedFrom":makeQuery(id+"F4.boolean.opBoolean","SPLIT",FACE,{"disambiguationData":[TD([makeQuery(id+"F4.opExtrude","SWEPT_FACE",FACE,{"disambiguationData":[OSD([subQ12])]})])],"derivedFrom":makeQuery(id+"F2.opExtrude","CAP_FACE",FACE,{"disambiguationData":[OSD([subQ13,subQ5,subQ14,sQuery(id+"F0.wireOp",EDGE,"E5")])],"isStart":false})})})});}
            var Q11;
            {var subQ1=sQuery(id+"F3.wireOp",EDGE,"E16.MirrorCS");var subQ2=makeQuery(id+"F4.opExtrude","SWEPT_FACE",FACE,{"disambiguationData":[OSD([subQ1])]});var subQ5=sQuery(id+"F0.wireOp",EDGE,"E2");var subQ13=sQuery(id+"F0.wireOp",EDGE,"E1");var subQ14=sQuery(id+"F0.wireOp",EDGE,"E3");Q11=makeQuery(id+"F8.boolean.opBoolean","SPLIT",FACE,{"disambiguationData":[TD([makeQuery(id+"F8.opExtrude","SWEPT_FACE",FACE,{"disambiguationData":[OSD([sQuery(id+"F6.wireOp",EDGE,"E65.0")])]})])],"derivedFrom":makeQuery(id+"F7.boolean.opBoolean","SPLIT",FACE,{"disambiguationData":[TD([makeQuery(id+"F4.boolean.opBoolean","COPY",FACE,{"derivedFrom":subQ2})])],"derivedFrom":makeQuery(id+"F4.boolean.opBoolean","SPLIT",FACE,{"disambiguationData":[TD([subQ2])],"derivedFrom":makeQuery(id+"F2.opExtrude","CAP_FACE",FACE,{"disambiguationData":[OSD([subQ13,subQ5,subQ14,sQuery(id+"F0.wireOp",EDGE,"E5")])],"isStart":false})})})});}
            chamfer(context, id + "F9", {"entities" : qUnion([Q0, Q1, Q2, Q3, Q4, Q5, Q6, Q7, Q8, Q9, Q10, Q11]), "width" : 12.7 * mm, "tangentPropagation" : true});
        }
        {
            var Q0;
            Q0=makeQuery(id+"F8.boolean.opBoolean","COPY",EDGE,{"derivedFrom":makeQuery(id+"F8.opExtrude","CAP_EDGE",EDGE,{"disambiguationData":[OSD([sQuery(id+"F6.wireOp",EDGE,"E74.MirrorCS")])],"isStart":true})});
            var Q1;
            Q1=makeQuery(id+"F8.boolean.opBoolean","COPY",EDGE,{"derivedFrom":makeQuery(id+"F8.opExtrude","CAP_EDGE",EDGE,{"disambiguationData":[OSD([sQuery(id+"F6.wireOp",EDGE,"E73.MirrorCS")])],"isStart":true})});
            var Q2;
            Q2=makeQuery(id+"F8.boolean.opBoolean","COPY",EDGE,{"derivedFrom":makeQuery(id+"F8.opExtrude","CAP_EDGE",EDGE,{"disambiguationData":[OSD([sQuery(id+"F6.wireOp",EDGE,"E79.MirrorCS")])],"isStart":true})});
            var Q3;
            Q3=makeQuery(id+"F8.boolean.opBoolean","COPY",EDGE,{"derivedFrom":makeQuery(id+"F8.opExtrude","CAP_EDGE",EDGE,{"disambiguationData":[OSD([sQuery(id+"F6.wireOp",EDGE,"E72.MirrorCS")])],"isStart":true})});
            var Q4;
            Q4=makeQuery(id+"F8.boolean.opBoolean","COPY",EDGE,{"derivedFrom":makeQuery(id+"F8.opExtrude","CAP_EDGE",EDGE,{"disambiguationData":[OSD([sQuery(id+"F6.wireOp",EDGE,"E71.MirrorCS")])],"isStart":true})});
            var Q5;
            Q5=makeQuery(id+"F8.boolean.opBoolean","COPY",EDGE,{"derivedFrom":makeQuery(id+"F8.opExtrude","CAP_EDGE",EDGE,{"disambiguationData":[OSD([sQuery(id+"F6.wireOp",EDGE,"E81.MirrorCS")])],"isStart":true})});
            var Q6;
            Q6=makeQuery(id+"F8.boolean.opBoolean","COPY",EDGE,{"derivedFrom":makeQuery(id+"F8.opExtrude","CAP_EDGE",EDGE,{"disambiguationData":[OSD([sQuery(id+"F6.wireOp",EDGE,"E83.MirrorCS")])],"isStart":true})});
            var Q7;
            Q7=makeQuery(id+"F8.boolean.opBoolean","COPY",EDGE,{"derivedFrom":makeQuery(id+"F8.opExtrude","CAP_EDGE",EDGE,{"disambiguationData":[OSD([sQuery(id+"F6.wireOp",EDGE,"E82.MirrorCS")])],"isStart":true})});
            var Q8;
            Q8=makeQuery(id+"F8.boolean.opBoolean","COPY",EDGE,{"derivedFrom":makeQuery(id+"F8.opExtrude","CAP_EDGE",EDGE,{"disambiguationData":[OSD([sQuery(id+"F6.wireOp",EDGE,"E85.MirrorCS")])],"isStart":true})});
            var Q9;
            Q9=makeQuery(id+"F8.boolean.opBoolean","COPY",EDGE,{"derivedFrom":makeQuery(id+"F8.opExtrude","CAP_EDGE",EDGE,{"disambiguationData":[OSD([sQuery(id+"F6.wireOp",EDGE,"E67.MirrorCS")])],"isStart":true})});
            var Q10;
            Q10=makeQuery(id+"F8.boolean.opBoolean","COPY",EDGE,{"derivedFrom":makeQuery(id+"F8.opExtrude","CAP_EDGE",EDGE,{"disambiguationData":[OSD([sQuery(id+"F6.wireOp",EDGE,"E78.MirrorCS")])],"isStart":true})});
            var Q11;
            Q11=makeQuery(id+"F8.boolean.opBoolean","COPY",EDGE,{"derivedFrom":makeQuery(id+"F8.opExtrude","CAP_EDGE",EDGE,{"disambiguationData":[OSD([sQuery(id+"F6.wireOp",EDGE,"E69.MirrorCS")])],"isStart":true})});
            var Q12;
            Q12=makeQuery(id+"F8.boolean.opBoolean","COPY",EDGE,{"derivedFrom":makeQuery(id+"F8.opExtrude","CAP_EDGE",EDGE,{"disambiguationData":[OSD([sQuery(id+"F6.wireOp",EDGE,"E62.top")])],"isStart":true})});
            var Q13;
            Q13=makeQuery(id+"F8.boolean.opBoolean","COPY",EDGE,{"derivedFrom":makeQuery(id+"F8.opExtrude","CAP_EDGE",EDGE,{"disambiguationData":[OSD([sQuery(id+"F6.wireOp",EDGE,"E62.left")])],"isStart":true})});
            var Q14;
            Q14=makeQuery(id+"F8.boolean.opBoolean","COPY",EDGE,{"derivedFrom":makeQuery(id+"F8.opExtrude","CAP_EDGE",EDGE,{"disambiguationData":[OSD([sQuery(id+"F6.wireOp",EDGE,"E62.right")])],"isStart":true})});
            var Q15;
            Q15=makeQuery(id+"F8.boolean.opBoolean","COPY",EDGE,{"derivedFrom":makeQuery(id+"F8.opExtrude","CAP_EDGE",EDGE,{"disambiguationData":[OSD([sQuery(id+"F6.wireOp",EDGE,"E62.bottom")])],"isStart":true})});
            var Q16;
            Q16=makeQuery(id+"F8.boolean.opBoolean","COPY",EDGE,{"derivedFrom":makeQuery(id+"F8.opExtrude","CAP_EDGE",EDGE,{"disambiguationData":[OSD([sQuery(id+"F5.wireOp",EDGE,"E52.MirrorCS")])],"isStart":true})});
            var Q17;
            Q17=makeQuery(id+"F8.boolean.opBoolean","COPY",EDGE,{"derivedFrom":makeQuery(id+"F8.opExtrude","CAP_EDGE",EDGE,{"disambiguationData":[OSD([sQuery(id+"F5.wireOp",EDGE,"E45.MirrorCS")])],"isStart":true})});
            var Q18;
            Q18=makeQuery(id+"F8.boolean.opBoolean","COPY",EDGE,{"derivedFrom":makeQuery(id+"F8.opExtrude","CAP_EDGE",EDGE,{"disambiguationData":[OSD([sQuery(id+"F5.wireOp",EDGE,"E34.MirrorCS")])],"isStart":true})});
            var Q19;
            Q19=makeQuery(id+"F8.boolean.opBoolean","COPY",EDGE,{"derivedFrom":makeQuery(id+"F8.opExtrude","CAP_EDGE",EDGE,{"disambiguationData":[OSD([sQuery(id+"F5.wireOp",EDGE,"E36.MirrorCS")])],"isStart":true})});
            var Q20;
            Q20=makeQuery(id+"F8.boolean.opBoolean","COPY",EDGE,{"derivedFrom":makeQuery(id+"F8.opExtrude","CAP_EDGE",EDGE,{"disambiguationData":[OSD([sQuery(id+"F5.wireOp",EDGE,"E29.top")])],"isStart":true})});
            var Q21;
            Q21=makeQuery(id+"F8.boolean.opBoolean","COPY",EDGE,{"derivedFrom":makeQuery(id+"F8.opExtrude","CAP_EDGE",EDGE,{"disambiguationData":[OSD([sQuery(id+"F5.wireOp",EDGE,"E29.right")])],"isStart":true})});
            var Q22;
            Q22=makeQuery(id+"F8.boolean.opBoolean","COPY",EDGE,{"derivedFrom":makeQuery(id+"F8.opExtrude","CAP_EDGE",EDGE,{"disambiguationData":[OSD([sQuery(id+"F5.wireOp",EDGE,"E29.left")])],"isStart":true})});
            var Q23;
            Q23=makeQuery(id+"F8.boolean.opBoolean","COPY",EDGE,{"derivedFrom":makeQuery(id+"F8.opExtrude","CAP_EDGE",EDGE,{"disambiguationData":[OSD([sQuery(id+"F5.wireOp",EDGE,"E29.bottom")])],"isStart":true})});
            var Q24;
            Q24=makeQuery(id+"F8.boolean.opBoolean","COPY",EDGE,{"derivedFrom":makeQuery(id+"F8.opExtrude","CAP_EDGE",EDGE,{"disambiguationData":[OSD([sQuery(id+"F5.wireOp",EDGE,"E28.top")])],"isStart":true})});
            var Q25;
            Q25=makeQuery(id+"F8.boolean.opBoolean","COPY",EDGE,{"derivedFrom":makeQuery(id+"F8.opExtrude","CAP_EDGE",EDGE,{"disambiguationData":[OSD([sQuery(id+"F5.wireOp",EDGE,"E28.left")])],"isStart":true})});
            var Q26;
            Q26=makeQuery(id+"F8.boolean.opBoolean","COPY",EDGE,{"derivedFrom":makeQuery(id+"F8.opExtrude","CAP_EDGE",EDGE,{"disambiguationData":[OSD([sQuery(id+"F5.wireOp",EDGE,"E28.right")])],"isStart":true})});
            var Q27;
            Q27=makeQuery(id+"F8.boolean.opBoolean","COPY",EDGE,{"derivedFrom":makeQuery(id+"F8.opExtrude","CAP_EDGE",EDGE,{"disambiguationData":[OSD([sQuery(id+"F5.wireOp",EDGE,"E28.bottom")])],"isStart":true})});
            var Q28;
            Q28=makeQuery(id+"F8.boolean.opBoolean","COPY",EDGE,{"derivedFrom":makeQuery(id+"F8.opExtrude","CAP_EDGE",EDGE,{"disambiguationData":[OSD([sQuery(id+"F5.wireOp",EDGE,"E38.MirrorCS")])],"isStart":true})});
            var Q29;
            Q29=makeQuery(id+"F8.boolean.opBoolean","COPY",EDGE,{"derivedFrom":makeQuery(id+"F8.opExtrude","CAP_EDGE",EDGE,{"disambiguationData":[OSD([sQuery(id+"F5.wireOp",EDGE,"E48.MirrorCS")])],"isStart":true})});
            var Q30;
            Q30=makeQuery(id+"F8.boolean.opBoolean","COPY",EDGE,{"derivedFrom":makeQuery(id+"F8.opExtrude","CAP_EDGE",EDGE,{"disambiguationData":[OSD([sQuery(id+"F5.wireOp",EDGE,"E50.MirrorCS")])],"isStart":true})});
            var Q31;
            Q31=makeQuery(id+"F8.boolean.opBoolean","COPY",EDGE,{"derivedFrom":makeQuery(id+"F8.opExtrude","CAP_EDGE",EDGE,{"disambiguationData":[OSD([sQuery(id+"F5.wireOp",EDGE,"E27.left")])],"isStart":true})});
            var Q32;
            Q32=makeQuery(id+"F8.boolean.opBoolean","COPY",EDGE,{"derivedFrom":makeQuery(id+"F8.opExtrude","CAP_EDGE",EDGE,{"disambiguationData":[OSD([sQuery(id+"F5.wireOp",EDGE,"E27.top")])],"isStart":true})});
            var Q33;
            Q33=makeQuery(id+"F8.boolean.opBoolean","COPY",EDGE,{"derivedFrom":makeQuery(id+"F8.opExtrude","CAP_EDGE",EDGE,{"disambiguationData":[OSD([sQuery(id+"F5.wireOp",EDGE,"E27.right")])],"isStart":true})});
            var Q34;
            Q34=makeQuery(id+"F8.boolean.opBoolean","COPY",EDGE,{"derivedFrom":makeQuery(id+"F8.opExtrude","CAP_EDGE",EDGE,{"disambiguationData":[OSD([sQuery(id+"F5.wireOp",EDGE,"E40.MirrorCS")])],"isStart":true})});
            var Q35;
            Q35=makeQuery(id+"F8.boolean.opBoolean","COPY",EDGE,{"derivedFrom":makeQuery(id+"F8.opExtrude","CAP_EDGE",EDGE,{"disambiguationData":[OSD([sQuery(id+"F5.wireOp",EDGE,"E41.MirrorCS")])],"isStart":true})});
            var Q36;
            Q36=makeQuery(id+"F8.boolean.opBoolean","COPY",EDGE,{"derivedFrom":makeQuery(id+"F8.opExtrude","CAP_EDGE",EDGE,{"disambiguationData":[OSD([sQuery(id+"F5.wireOp",EDGE,"E39.MirrorCS")])],"isStart":true})});
            var Q37;
            Q37=makeQuery(id+"F8.boolean.opBoolean","COPY",EDGE,{"derivedFrom":makeQuery(id+"F8.opExtrude","CAP_EDGE",EDGE,{"disambiguationData":[OSD([sQuery(id+"F5.wireOp",EDGE,"E49.MirrorCS")])],"isStart":true})});
            var Q38;
            Q38=makeQuery(id+"F8.boolean.opBoolean","COPY",EDGE,{"derivedFrom":makeQuery(id+"F8.opExtrude","CAP_EDGE",EDGE,{"disambiguationData":[OSD([sQuery(id+"F6.wireOp",EDGE,"E61.left")])],"isStart":true})});
            var Q39;
            Q39=makeQuery(id+"F8.boolean.opBoolean","COPY",EDGE,{"derivedFrom":makeQuery(id+"F8.opExtrude","CAP_EDGE",EDGE,{"disambiguationData":[OSD([sQuery(id+"F6.wireOp",EDGE,"E61.top")])],"isStart":true})});
            var Q40;
            Q40=makeQuery(id+"F8.boolean.opBoolean","COPY",EDGE,{"derivedFrom":makeQuery(id+"F8.opExtrude","CAP_EDGE",EDGE,{"disambiguationData":[OSD([sQuery(id+"F6.wireOp",EDGE,"E61.right")])],"isStart":true})});
            var Q41;
            Q41=makeQuery(id+"F8.boolean.opBoolean","COPY",EDGE,{"derivedFrom":makeQuery(id+"F8.opExtrude","CAP_EDGE",EDGE,{"disambiguationData":[OSD([sQuery(id+"F6.wireOp",EDGE,"E61.bottom")])],"isStart":true})});
            var Q42;
            Q42=makeQuery(id+"F8.boolean.opBoolean","COPY",EDGE,{"derivedFrom":makeQuery(id+"F8.opExtrude","CAP_EDGE",EDGE,{"disambiguationData":[OSD([sQuery(id+"F6.wireOp",EDGE,"E60.top")])],"isStart":true})});
            var Q43;
            Q43=makeQuery(id+"F8.boolean.opBoolean","COPY",EDGE,{"derivedFrom":makeQuery(id+"F8.opExtrude","CAP_EDGE",EDGE,{"disambiguationData":[OSD([sQuery(id+"F6.wireOp",EDGE,"E60.left")])],"isStart":true})});
            var Q44;
            Q44=makeQuery(id+"F8.boolean.opBoolean","COPY",EDGE,{"derivedFrom":makeQuery(id+"F8.opExtrude","CAP_EDGE",EDGE,{"disambiguationData":[OSD([sQuery(id+"F6.wireOp",EDGE,"E60.bottom")])],"isStart":true})});
            var Q45;
            Q45=makeQuery(id+"F8.boolean.opBoolean","COPY",EDGE,{"derivedFrom":makeQuery(id+"F8.opExtrude","CAP_EDGE",EDGE,{"disambiguationData":[OSD([sQuery(id+"F6.wireOp",EDGE,"E60.right")])],"isStart":true})});
            var Q46;
            Q46=makeQuery(id+"F8.boolean.opBoolean","COPY",EDGE,{"derivedFrom":makeQuery(id+"F8.opExtrude","CAP_EDGE",EDGE,{"disambiguationData":[OSD([sQuery(id+"F5.wireOp",EDGE,"E46.MirrorCS")])],"isStart":true})});
            var Q47;
            Q47=makeQuery(id+"F8.boolean.opBoolean","COPY",EDGE,{"derivedFrom":makeQuery(id+"F8.opExtrude","CAP_EDGE",EDGE,{"disambiguationData":[OSD([sQuery(id+"F5.wireOp",EDGE,"E27.bottom")])],"isStart":true})});
            chamfer(context, id + "F10", {"entities" : qUnion([Q0, Q1, Q2, Q3, Q4, Q5, Q6, Q7, Q8, Q9, Q10, Q11, Q12, Q13, Q14, Q15, Q16, Q17, Q18, Q19, Q20, Q21, Q22, Q23, Q24, Q25, Q26, Q27, Q28, Q29, Q30, Q31, Q32, Q33, Q34, Q35, Q36, Q37, Q38, Q39, Q40, Q41, Q42, Q43, Q44, Q45, Q46, Q47]), "width" : 12.7 * mm, "tangentPropagation" : true});
        }
        {
            var Q0;
            {var subQ10=sQuery(id+"F0.wireOp",EDGE,"E2");var subQ11=makeQuery(id+"F1.opExtrude","SWEPT_FACE",FACE,{"disambiguationData":[OSD([subQ10])]});var subQ14=sQuery(id+"F3.wireOp",EDGE,"E11");var subQ15=makeQuery(id+"F4.opExtrude","SWEPT_FACE",FACE,{"disambiguationData":[OSD([subQ14])]});var subQ16=makeQuery(id+"F4.boolean.opBoolean","COPY",FACE,{"derivedFrom":subQ15});var subQ20=sQuery(id+"F0.wireOp",EDGE,"E1");var subQ21=sQuery(id+"F0.wireOp",EDGE,"E3");Q0=makeQuery(id+"F8.boolean.opBoolean","SPLIT",FACE,{"disambiguationData":[TD([subQ11])],"derivedFrom":makeQuery(id+"F7.boolean.opBoolean","SPLIT",FACE,{"disambiguationData":[TD([subQ16])],"derivedFrom":makeQuery(id+"F4.boolean.opBoolean","SPLIT",FACE,{"disambiguationData":[TD([makeQuery(id+"F4.opExtrude","SWEPT_FACE",FACE,{"disambiguationData":[OSD([sQuery(id+"F3.wireOp",EDGE,"E6")])]})])],"derivedFrom":makeQuery(id+"F2.opExtrude","CAP_FACE",FACE,{"disambiguationData":[OSD([subQ20,subQ10,subQ21,sQuery(id+"F0.wireOp",EDGE,"E5")])],"isStart":false})})})});}
            var sketch = newSketch(context, id + "F11", { "sketchPlane" : qUnion([Q0])});
            skCircle(sketch, "E93", {"center": v(-189.7, -136.52) * mm, "radius": 6.35 * mm});
            skSolve(sketch);
        }
        {
            var Q0;
            Q0=makeQuery(id+"F11.imprint","IMPRINT",FACE,{"disambiguationData":[TD([[makeQuery(id+"F11.imprint","IMPRINT",EDGE,{"derivedFrom":sQuery(id+"F11.wireOp",EDGE,"E93")}),1.0]])]});
            extrude(context, id + "F12", {"entities" : qUnion([Q0]), "operationType" : NewBodyOperationType.ADD, "depth" : 12.7 * mm, "offsetDistance" : 25.4 * mm});
        }
        {
            var Q0;
            Q0=makeQuery(id+"F12.opExtrude","CAP_FACE",FACE,{"disambiguationData":[OSD([sQuery(id+"F11.wireOp",EDGE,"E93")])],"isStart":false});
            var sketch = newSketch(context, id + "F13", { "sketchPlane" : qUnion([Q0])});
            skCircle(sketch, "E94", {"center": v(-189.7, -136.52) * mm, "radius": 22.23 * mm});
            skSolve(sketch);
        }
        {
            var Q0;
            Q0 = qSketchRegion(id + "F13", true);
            extrude(context, id + "F14", {"entities" : qUnion([Q0]), "operationType" : NewBodyOperationType.ADD, "depth" : 3.17 * mm, "offsetDistance" : 25.4 * mm});
        }
        {
            var Q0;
            {var subQ3=sQuery(id+"F0.wireOp",EDGE,"E2");var subQ4=makeQuery(id+"F1.opExtrude","SWEPT_FACE",FACE,{"disambiguationData":[OSD([subQ3])]});var subQ12=sQuery(id+"F3.wireOp",EDGE,"E16.MirrorCS");var subQ13=makeQuery(id+"F4.opExtrude","SWEPT_FACE",FACE,{"disambiguationData":[OSD([subQ12])]});var subQ14=makeQuery(id+"F4.boolean.opBoolean","COPY",FACE,{"derivedFrom":subQ13});var subQ20=sQuery(id+"F0.wireOp",EDGE,"E1");var subQ21=sQuery(id+"F0.wireOp",EDGE,"E3");Q0=makeQuery(id+"F8.boolean.opBoolean","SPLIT",FACE,{"disambiguationData":[TD([subQ4])],"derivedFrom":makeQuery(id+"F7.boolean.opBoolean","SPLIT",FACE,{"disambiguationData":[TD([subQ14])],"derivedFrom":makeQuery(id+"F4.boolean.opBoolean","SPLIT",FACE,{"disambiguationData":[TD([subQ13])],"derivedFrom":makeQuery(id+"F2.opExtrude","CAP_FACE",FACE,{"disambiguationData":[OSD([subQ20,subQ3,subQ21,sQuery(id+"F0.wireOp",EDGE,"E5")])],"isStart":false})})})});}
            var sketch = newSketch(context, id + "F15", { "sketchPlane" : qUnion([Q0])});
            skCircle(sketch, "E95", {"center": v(189.71, -136.52) * mm, "radius": 6.35 * mm});
            skSolve(sketch);
        }
        {
            var Q0;
            Q0 = qSketchRegion(id + "F15", true);
            extrude(context, id + "F16", {"entities" : qUnion([Q0]), "operationType" : NewBodyOperationType.ADD, "depth" : 12.7 * mm, "offsetDistance" : 25.4 * mm});
        }
        {
            var Q0;
            Q0=makeQuery(id+"F16.opExtrude","CAP_FACE",FACE,{"disambiguationData":[OSD([sQuery(id+"F15.wireOp",EDGE,"E95")])],"isStart":false});
            var sketch = newSketch(context, id + "F17", { "sketchPlane" : qUnion([Q0])});
            skCircle(sketch, "E96", {"center": v(189.71, -136.52) * mm, "radius": 22.23 * mm});
            skSolve(sketch);
        }
        {
            var Q0;
            Q0 = qSketchRegion(id + "F17", true);
            extrude(context, id + "F18", {"entities" : qUnion([Q0]), "operationType" : NewBodyOperationType.ADD, "depth" : 3.17 * mm, "offsetDistance" : 25.4 * mm});
        }
        {
            var Q0;
            Q0=makeQuery(id+"F14.opExtrude","CAP_FACE",FACE,{"disambiguationData":[OSD([sQuery(id+"F13.wireOp",EDGE,"E94")])],"isStart":false});
            var Q1;
            Q1=makeQuery(id+"F18.opExtrude","CAP_FACE",FACE,{"disambiguationData":[OSD([sQuery(id+"F17.wireOp",EDGE,"E96")])],"isStart":false});
            fillet(context, id + "F19", {"entities" : qUnion([Q0, Q1]), "radius" : 5.08 * mm, "tangentPropagation" : true, "allowEdgeOverflow" : false});
        }
    });
